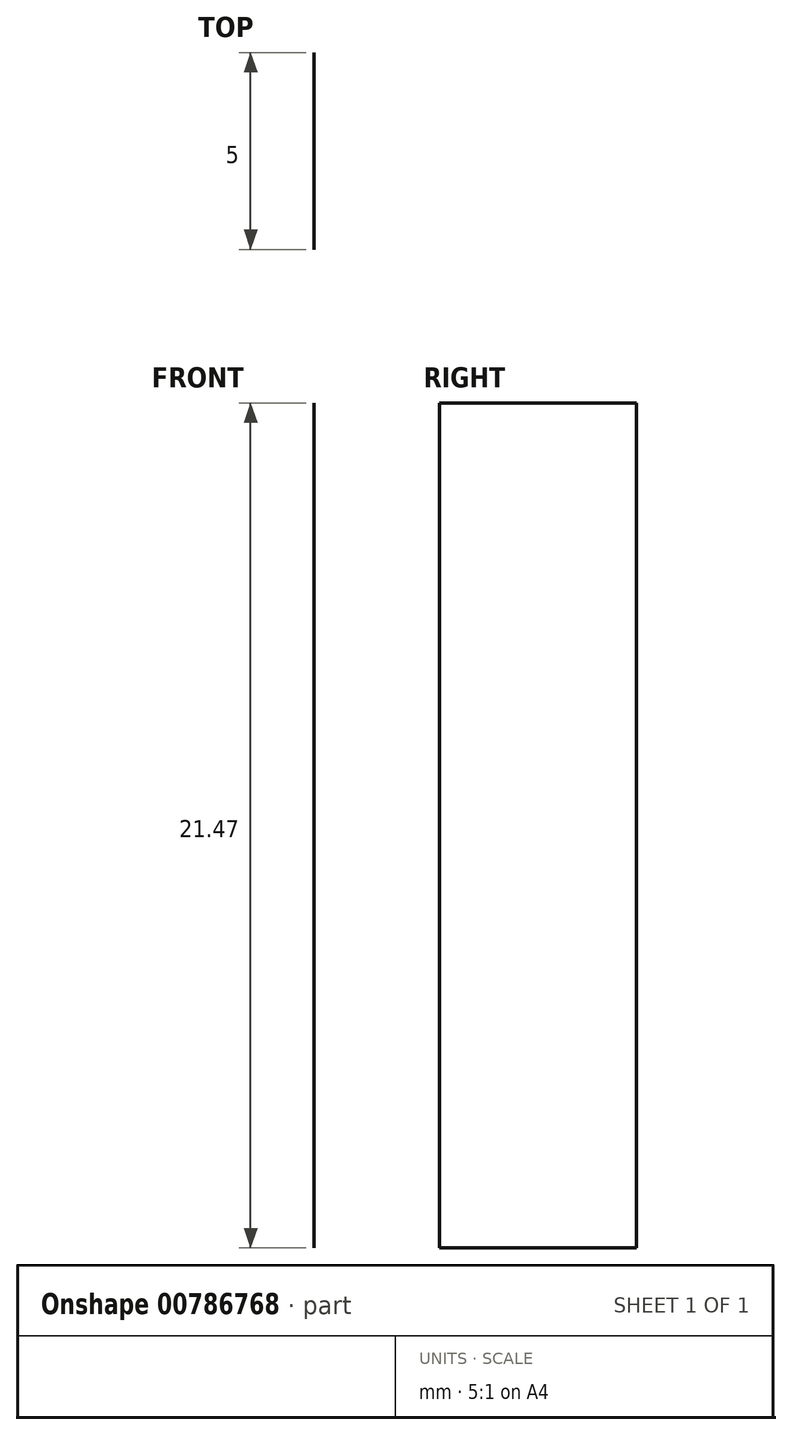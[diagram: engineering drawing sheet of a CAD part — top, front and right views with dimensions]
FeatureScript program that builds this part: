
annotation { "Feature Type Name" : "Feature", "Feature Type Description" : "" }
export const myFeature = defineFeature(function(context is Context, id is Id, definition is map)
    precondition{}
    {
        {
            var Q0;
            Q0=qCreatedBy(makeId("Front.planeOp"),FACE);
            var sketch = newSketch(context, id + "F0", { "sketchPlane" : qUnion([Q0])});
            skLineSegment(sketch, "E0.bottom", {"start": v(0, 0) * mm, "end": v(42.61, 0) * mm});
            skLineSegment(sketch, "E0.top", {"start": v(0, 21.47) * mm, "end": v(42.61, 21.47) * mm});
            skLineSegment(sketch, "E0.left", {"start": v(0, 0) * mm, "end": v(0, 21.47) * mm});
            skLineSegment(sketch, "E0.right", {"start": v(42.61, 0) * mm, "end": v(42.61, 21.47) * mm});
            skSolve(sketch);
        }
        {
            var Q0;
            Q0=sQuery(id+"F0.wireOp",EDGE,"E0.right");
            extrude(context, id + "F1", {"bodyType" : ToolBodyType.SURFACE, "surfaceEntities" : qUnion([Q0]), "depth" : 5 * mm, "offsetDistance" : 25.4 * mm});
        }
    });
